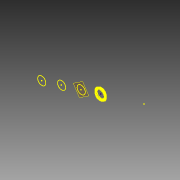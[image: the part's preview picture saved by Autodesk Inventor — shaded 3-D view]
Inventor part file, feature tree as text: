
AUTODESK INVENTOR PART (.ipt)
format: ipt  version: 2015 (Build 190159000, 159)  size: 80,384 bytes
history: native  units: in
note: dims shown in document units (in); Inventor stores cm internally (conversion verified against a paired STEP export)
features: reference x5, plane x1, sketch x1
ambient origin geometry x8: Origin, YZ Plane, XZ Plane, XY Plane, X Axis, Y Axis, Z Axis, Center Point
feature tree (7):
  plane  "Work Plane1"
  sketch  "Sketch1"
  reference  "Reference1"
  reference  "Reference2"
  reference  "Reference3"
  reference  "Reference4"
  reference  "Reference5"
